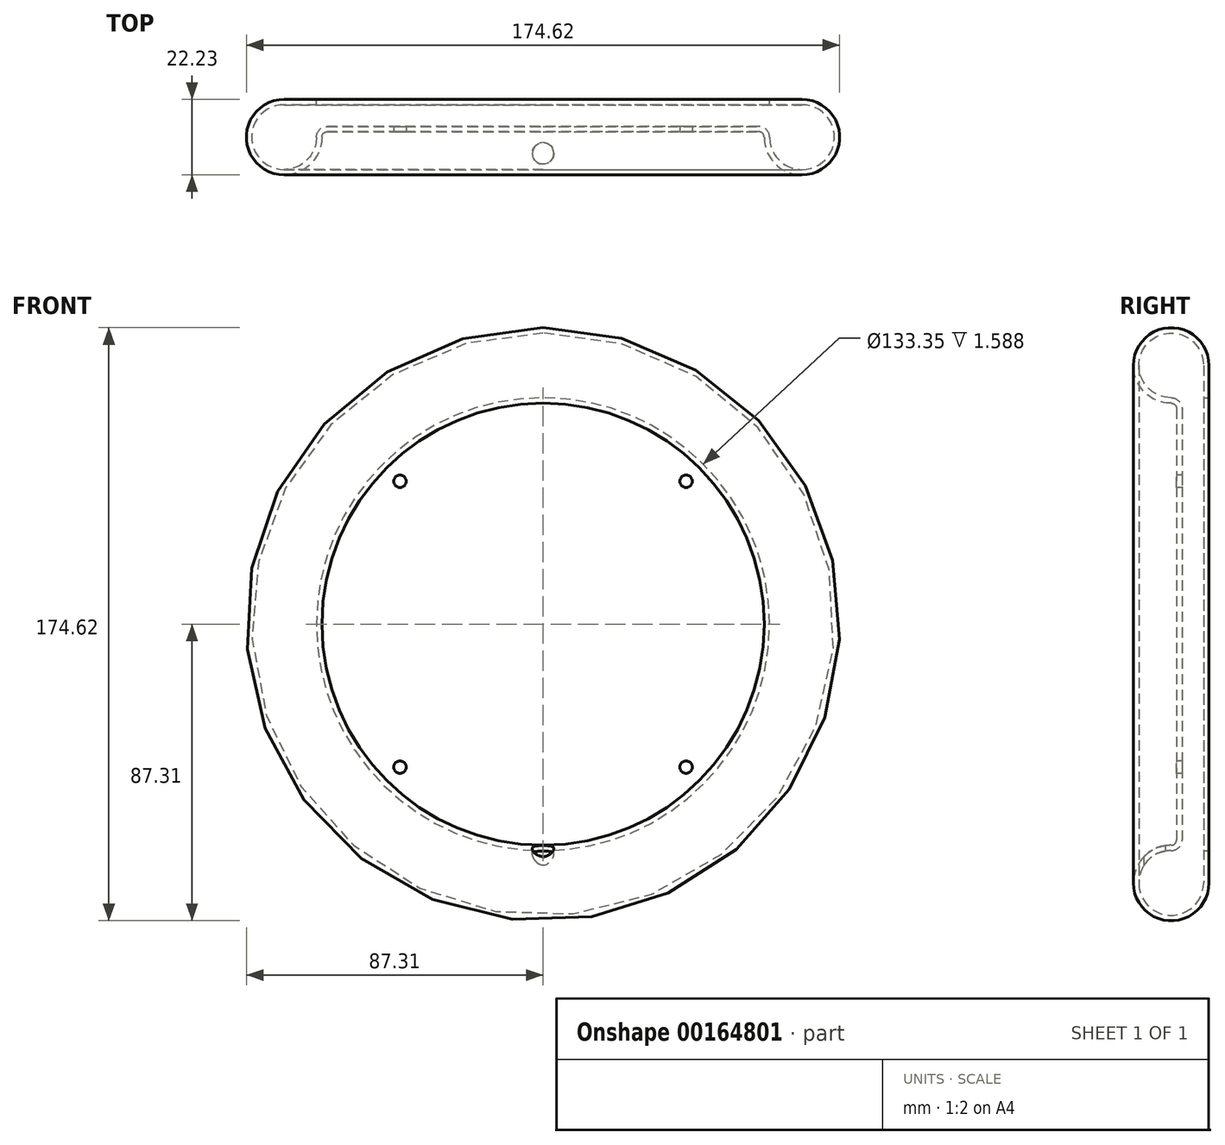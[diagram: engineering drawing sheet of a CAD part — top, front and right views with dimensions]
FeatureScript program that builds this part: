
annotation { "Feature Type Name" : "Feature", "Feature Type Description" : "" }
export const myFeature = defineFeature(function(context is Context, id is Id, definition is map)
    precondition{}
    {
        {
            var Q0;
            Q0=qCreatedBy(makeId("Top.planeOp"),FACE);
            var sketch = newSketch(context, id + "F0", { "sketchPlane" : qUnion([Q0])});
            skLineSegment(sketch, "E0", {"start": v(0, 0) * mm, "end": v(76.2, 0) * mm});
            skLineSegment(sketch, "E1", {"start": v(0, 0) * mm, "end": v(0, 1.59) * mm});
            skArc(sketch, "E2", {"start": v(66.68, -9.52) * mm, "mid": v(82.94, -16.26) * mm, "end": v(76.2, 0) * mm});
            skLineSegment(sketch, "E3", {"start": v(0, 1.59) * mm, "end": v(76.2, 1.59) * mm});
            skLineSegment(sketch, "E4", {"start": v(76.2, 0) * mm, "end": v(76.2, 1.59) * mm, "construction": true});
            skLineSegment(sketch, "E5", {"start": v(0, 0) * mm, "end": v(0, -6.35) * mm, "construction": true});
            skLineSegment(sketch, "E6.bottom", {"start": v(0, -6.35) * mm, "end": v(63.5, -6.35) * mm});
            skLineSegment(sketch, "E6.top", {"start": v(0, -7.94) * mm, "end": v(63.5, -7.94) * mm});
            skLineSegment(sketch, "E6.left", {"start": v(0, -6.35) * mm, "end": v(0, -7.94) * mm});
            skLineSegment(sketch, "E6.right", {"start": v(63.5, -6.35) * mm, "end": v(63.5, -7.94) * mm});
            skArc(sketch, "E7", {"start": v(66.68, -9.52) * mm, "mid": v(65.75, -7.28) * mm, "end": v(63.5, -6.35) * mm});
            skArc(sketch, "E8", {"start": v(65.09, -9.52) * mm, "mid": v(64.62, -8.4) * mm, "end": v(63.5, -7.94) * mm});
            skArc(sketch, "E9", {"start": v(65.09, -9.52) * mm, "mid": v(84.06, -17.38) * mm, "end": v(76.2, 1.59) * mm});
            skLineSegment(sketch, "E10", {"start": v(0, -7.94) * mm, "end": v(0, -20.64) * mm, "construction": true});
            skLineSegment(sketch, "E11", {"start": v(0, -20.64) * mm, "end": v(76.2, -20.64) * mm, "construction": true});
            skLineSegment(sketch, "E12", {"start": v(76.2, -9.52) * mm, "end": v(76.2, -6.35) * mm, "construction": true});
            skLineSegment(sketch, "E13", {"start": v(76.2, -6.35) * mm, "end": v(63.5, -6.35) * mm, "construction": true});
            skSolve(sketch);
        }
        {
            var Q0;
            Q0=qCreatedBy(makeId("Front.planeOp"),FACE);
            var sketch = newSketch(context, id + "F1", { "sketchPlane" : qUnion([Q0])});
            skCircle(sketch, "E14", {"center": v(0, 0) * mm, "radius": 12.7 * mm});
            skSolve(sketch);
        }
        {
            var Q0;
            Q0=makeQuery(id+"F0.imprint","IMPRINT",FACE,{"disambiguationData":[TD([[makeQuery(id+"F0.imprint","IMPRINT",EDGE,{"derivedFrom":sQuery(id+"F0.wireOp",EDGE,"E0")}),1.0]])]});
            var Q1;
            Q1=makeQuery(id+"F0.imprint","IMPRINT",FACE,{"disambiguationData":[TD([[makeQuery(id+"F0.imprint","IMPRINT",EDGE,{"derivedFrom":sQuery(id+"F0.wireOp",EDGE,"E6.bottom")}),-1.0]])]});
            var Q2;
            Q2=sQuery(id+"F1.wireOp",EDGE,"E14");
            revolve(context, id + "F2", {"entities" : qUnion([Q0, Q1]), "axis" : qUnion([Q2]), "revolveType" : RevolveType.FULL});
        }
        {
            var Q0;
            Q0=makeQuery(id+"F2.opRevolve","SWEPT_FACE",FACE,{"disambiguationData":[OSD([sQuery(id+"F0.wireOp",EDGE,"E3")])]});
            var sketch = newSketch(context, id + "F3", { "sketchPlane" : qUnion([Q0])});
            skCircle(sketch, "E15", {"center": v(0, 0) * mm, "radius": 66.67 * mm});
            skSolve(sketch);
        }
        {
            var Q0;
            Q0=qSketchRegion(id+"F3",true);
            extrude(context, id + "F4", {"entities" : qUnion([Q0]), "operationType" : NewBodyOperationType.REMOVE, "oppositeDirection" : true, "depth" : 1.59 * mm});
        }
        {
            var Q0;
            Q0=qCreatedBy(makeId("Top.planeOp"),FACE);
            var sketch = newSketch(context, id + "F5", { "sketchPlane" : qUnion([Q0])});
            skLineSegment(sketch, "E16", {"start": v(0, -7.94) * mm, "end": v(0, -14.29) * mm, "construction": true});
            skCircle(sketch, "E17", {"center": v(0, -14.29) * mm, "radius": 3.18 * mm});
            skSolve(sketch);
        }
        {
            var Q0;
            Q0=qSketchRegion(id+"F5",true);
            var Q1;
            Q1=makeQuery(id+"F2.opRevolve","SWEPT_FACE",FACE,{"disambiguationData":[OSD([sQuery(id+"F0.wireOp",EDGE,"E2")])]});
            extrude(context, id + "F6", {"entities" : qUnion([Q0]), "operationType" : NewBodyOperationType.REMOVE, "endBound" : BoundingType.UP_TO_SURFACE, "oppositeDirection" : true, "endBoundEntityFace" : qUnion([Q1]), "depth" : 25.4 * mm});
        }
        {
            var Q0;
            Q0=makeQuery(id+"F2.opRevolve","SWEPT_FACE",FACE,{"disambiguationData":[OSD([sQuery(id+"F0.wireOp",EDGE,"E6.top")])]});
            var sketch = newSketch(context, id + "F7", { "sketchPlane" : qUnion([Q0])});
            skCircle(sketch, "E18", {"center": v(42.1, -42.1) * mm, "radius": 3.97 * mm, "construction": true});
            skLineSegment(sketch, "E19.bottom", {"start": v(42.1, -42.1) * mm, "end": v(-42.1, -42.1) * mm, "construction": true});
            skLineSegment(sketch, "E19.top", {"start": v(42.1, 42.1) * mm, "end": v(-42.1, 42.1) * mm, "construction": true});
            skLineSegment(sketch, "E19.left", {"start": v(42.1, -42.1) * mm, "end": v(42.1, 42.1) * mm, "construction": true});
            skLineSegment(sketch, "E19.right", {"start": v(-42.1, -42.1) * mm, "end": v(-42.1, 42.1) * mm, "construction": true});
            skPoint(sketch, "E19.middle", {"position": v(0, 0) * mm});
            skCircle(sketch, "E20", {"center": v(42.1, -42.1) * mm, "radius": 1.83 * mm});
            skCircle(sketch, "E21", {"center": v(-42.1, -42.1) * mm, "radius": 1.83 * mm});
            skCircle(sketch, "E22", {"center": v(-42.1, 42.1) * mm, "radius": 1.83 * mm});
            skCircle(sketch, "E23", {"center": v(42.1, 42.1) * mm, "radius": 1.83 * mm});
            skSolve(sketch);
        }
        {
            var Q0;
            Q0=qSketchRegion(id+"F7",true);
            var Q1;
            Q1=makeQuery(id+"F2.opRevolve","SWEPT_FACE",FACE,{"disambiguationData":[OSD([sQuery(id+"F0.wireOp",EDGE,"E6.bottom")])]});
            extrude(context, id + "F8", {"entities" : qUnion([Q0]), "operationType" : NewBodyOperationType.REMOVE, "endBound" : BoundingType.UP_TO_SURFACE, "oppositeDirection" : true, "endBoundEntityFace" : qUnion([Q1]), "depth" : 25.4 * mm});
        }
    });
